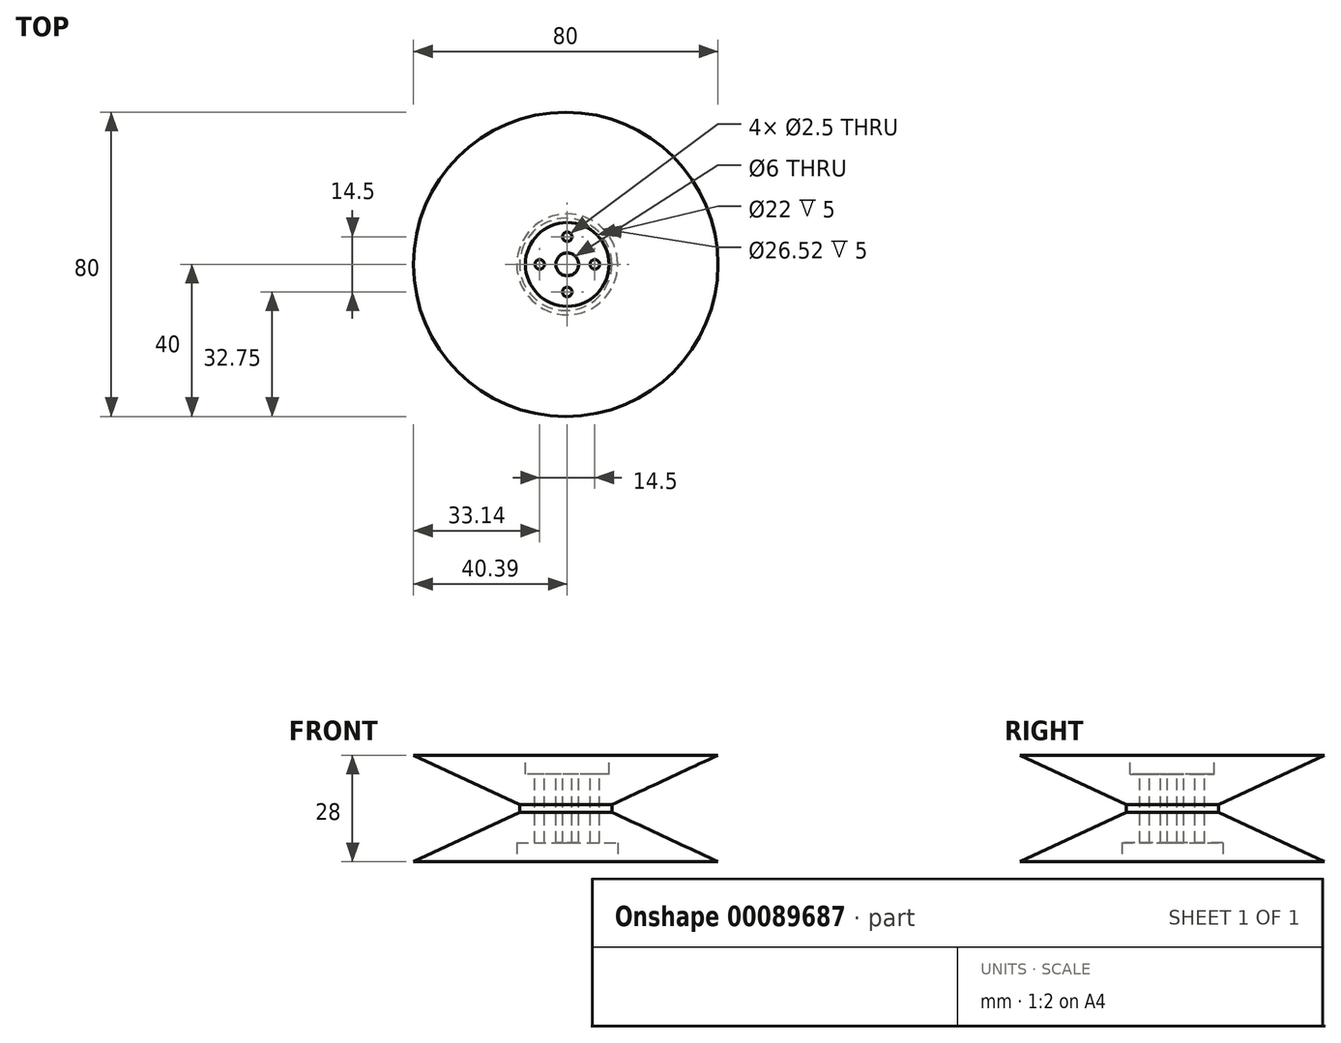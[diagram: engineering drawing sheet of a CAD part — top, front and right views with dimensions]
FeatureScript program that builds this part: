
annotation { "Feature Type Name" : "Feature", "Feature Type Description" : "" }
export const myFeature = defineFeature(function(context is Context, id is Id, definition is map)
    precondition{}
    {
        {
            var Q0;
            Q0=qCreatedBy(makeId("Top.planeOp"),FACE);
            var sketch = newSketch(context, id + "F0", { "sketchPlane" : qUnion([Q0])});
            skCircle(sketch, "E0", {"center": v(-0.4, 0) * mm, "radius": 40 * mm});
            skSolve(sketch);
        }
        {
            var Q0;
            Q0=makeQuery(id+"F0.imprint","IMPRINT",FACE,{"disambiguationData":[TD([[makeQuery(id+"F0.imprint","IMPRINT",EDGE,{"derivedFrom":sQuery(id+"F0.wireOp",EDGE,"E0")}),1.0]])]});
            extrude(context, id + "F1", {"entities" : qUnion([Q0]), "depth" : 13 * mm, "hasDraft" : true, "draftAngle" : 65 * degree, "draftPullDirection" : true});
        }
        {
            var Q0;
            Q0=makeQuery(id+"F1.opExtrude","CAP_FACE",FACE,{"disambiguationData":[OSD([sQuery(id+"F0.wireOp",EDGE,"E0")])],"isStart":false});
            extrude(context, id + "F2", {"entities" : qUnion([Q0]), "operationType" : NewBodyOperationType.ADD, "depth" : 2 * mm});
        }
        {
            var Q0;
            Q0=makeQuery(id+"F2.opExtrude","CAP_FACE",FACE,{"disambiguationData":[OSD([sQuery(id+"F0.wireOp",EDGE,"E0")])],"isStart":false});
            extrude(context, id + "F3", {"entities" : qUnion([Q0]), "operationType" : NewBodyOperationType.ADD, "depth" : 13 * mm, "hasDraft" : true, "draftAngle" : 65 * degree});
        }
        {
            var Q0;
            Q0=makeQuery(id+"F3.opExtrude","CAP_FACE",FACE,{"disambiguationData":[OSD([sQuery(id+"F0.wireOp",EDGE,"E0")])],"isStart":false});
            var sketch = newSketch(context, id + "F4", { "sketchPlane" : qUnion([Q0])});
            skCircle(sketch, "E1", {"center": v(0, 0) * mm, "radius": 11 * mm});
            skSolve(sketch);
        }
        {
            var Q0;
            Q0=makeQuery(id+"F4.imprint","IMPRINT",FACE,{"disambiguationData":[TD([[makeQuery(id+"F4.imprint","IMPRINT",EDGE,{"derivedFrom":sQuery(id+"F4.wireOp",EDGE,"E1")}),1.0]])]});
            extrude(context, id + "F5", {"entities" : qUnion([Q0]), "operationType" : NewBodyOperationType.REMOVE, "oppositeDirection" : true, "depth" : 5 * mm});
        }
        {
            var Q0;
            Q0=makeQuery(id+"F5.boolean.opBoolean","COPY",FACE,{"derivedFrom":makeQuery(id+"F5.opExtrude","CAP_FACE",FACE,{"disambiguationData":[OSD([sQuery(id+"F4.wireOp",EDGE,"E1")])],"isStart":false})});
            var sketch = newSketch(context, id + "F6", { "sketchPlane" : qUnion([Q0])});
            skCircle(sketch, "E2", {"center": v(0, 0) * mm, "radius": 3 * mm});
            skCircle(sketch, "E3", {"center": v(0, 7.25) * mm, "radius": 1.25 * mm});
            skCircle(sketch, "E4", {"center": v(0, -7.25) * mm, "radius": 1.25 * mm});
            skCircle(sketch, "E5", {"center": v(7.25, 0) * mm, "radius": 1.25 * mm});
            skCircle(sketch, "E6", {"center": v(-7.25, 0) * mm, "radius": 1.25 * mm});
            skSolve(sketch);
        }
        {
            var Q0;
            Q0=makeQuery(id+"F6.imprint","IMPRINT",FACE,{"disambiguationData":[TD([[makeQuery(id+"F6.imprint","IMPRINT",EDGE,{"derivedFrom":sQuery(id+"F6.wireOp",EDGE,"E2")}),1.0]])]});
            extrude(context, id + "F7", {"entities" : qUnion([Q0]), "operationType" : NewBodyOperationType.REMOVE, "oppositeDirection" : true, "depth" : 50 * mm});
        }
        {
            var Q0;
            Q0=makeQuery(id+"F6.imprint","IMPRINT",FACE,{"disambiguationData":[TD([[makeQuery(id+"F6.imprint","IMPRINT",EDGE,{"derivedFrom":sQuery(id+"F6.wireOp",EDGE,"E3")}),1.0]])]});
            var Q1;
            Q1=makeQuery(id+"F6.imprint","IMPRINT",FACE,{"disambiguationData":[TD([[makeQuery(id+"F6.imprint","IMPRINT",EDGE,{"derivedFrom":sQuery(id+"F6.wireOp",EDGE,"E5")}),1.0]])]});
            var Q2;
            Q2=makeQuery(id+"F6.imprint","IMPRINT",FACE,{"disambiguationData":[TD([[makeQuery(id+"F6.imprint","IMPRINT",EDGE,{"derivedFrom":sQuery(id+"F6.wireOp",EDGE,"E4")}),1.0]])]});
            var Q3;
            Q3=makeQuery(id+"F6.imprint","IMPRINT",FACE,{"disambiguationData":[TD([[makeQuery(id+"F6.imprint","IMPRINT",EDGE,{"derivedFrom":sQuery(id+"F6.wireOp",EDGE,"E6")}),1.0]])]});
            extrude(context, id + "F8", {"entities" : qUnion([Q0, Q1, Q2, Q3]), "operationType" : NewBodyOperationType.REMOVE, "oppositeDirection" : true, "depth" : 20 * mm});
        }
        {
            var Q0;
            Q0=makeQuery(id+"F1.opExtrude","CAP_FACE",FACE,{"disambiguationData":[OSD([sQuery(id+"F0.wireOp",EDGE,"E0")])],"isStart":true});
            var sketch = newSketch(context, id + "F9", { "sketchPlane" : qUnion([Q0])});
            skCircle(sketch, "E7", {"center": v(0, 0) * mm, "radius": 13.26 * mm});
            skSolve(sketch);
        }
        {
            var Q0;
            Q0=makeQuery(id+"F9.imprint","IMPRINT",FACE,{"disambiguationData":[TD([[makeQuery(id+"F9.imprint","IMPRINT",EDGE,{"derivedFrom":sQuery(id+"F9.wireOp",EDGE,"E7")}),1.0]])]});
            extrude(context, id + "F10", {"entities" : qUnion([Q0]), "operationType" : NewBodyOperationType.REMOVE, "oppositeDirection" : true, "depth" : 5 * mm});
        }
    });
